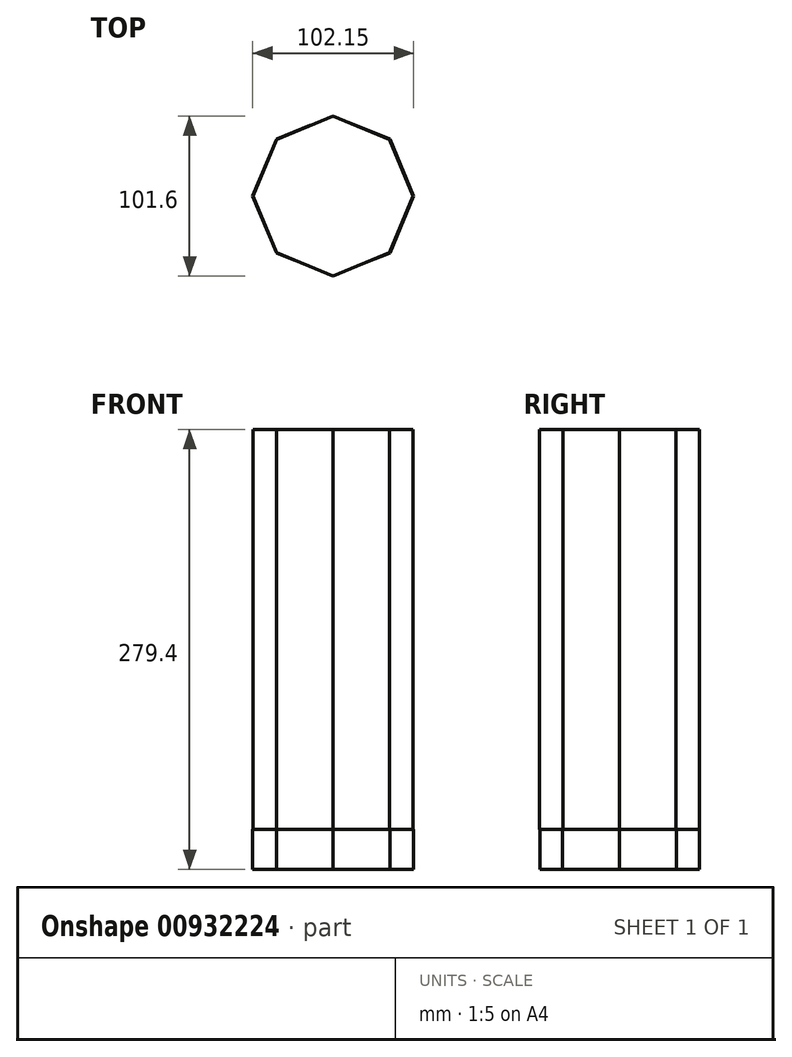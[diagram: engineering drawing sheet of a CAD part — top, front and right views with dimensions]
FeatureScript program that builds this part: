
annotation { "Feature Type Name" : "Feature", "Feature Type Description" : "" }
export const myFeature = defineFeature(function(context is Context, id is Id, definition is map)
    precondition{}
    {
        {
            var Q0;
            Q0=qCreatedBy(makeId("Top.planeOp"),FACE);
            var sketch = newSketch(context, id + "F0", { "sketchPlane" : qUnion([Q0])});
            skCircle(sketch, "E0.cCircle", {"center": v(0, 0) * mm, "radius": 50.8 * mm, "construction": true});
            skLineSegment(sketch, "E0.0", {"start": v(50.8, 0) * mm, "end": v(35.92, -35.92) * mm});
            skLineSegment(sketch, "E0.1", {"start": v(35.92, -35.92) * mm, "end": v(0, -50.8) * mm});
            skLineSegment(sketch, "E0.2", {"start": v(0, -50.8) * mm, "end": v(-35.92, -35.92) * mm});
            skLineSegment(sketch, "E0.3", {"start": v(-35.92, -35.92) * mm, "end": v(-50.8, 0) * mm});
            skLineSegment(sketch, "E0.4", {"start": v(-50.8, 0) * mm, "end": v(-35.92, 35.92) * mm});
            skLineSegment(sketch, "E0.5", {"start": v(-35.92, 35.92) * mm, "end": v(0, 50.8) * mm});
            skLineSegment(sketch, "E0.6", {"start": v(0, 50.8) * mm, "end": v(35.92, 35.92) * mm});
            skLineSegment(sketch, "E0.7", {"start": v(35.92, 35.92) * mm, "end": v(50.8, 0) * mm});
            skSolve(sketch);
        }
        {
            var Q0;
            Q0=makeQuery(id+"F0.imprint","IMPRINT",FACE,{"disambiguationData":[TD([[makeQuery(id+"F0.imprint","IMPRINT",EDGE,{"derivedFrom":sQuery(id+"F0.wireOp",EDGE,"E0.0")}),-1.0]])]});
            extrude(context, id + "F1", {"entities" : qUnion([Q0]), "depth" : 254 * mm, "offsetDistance" : 25.4 * mm});
        }
        {
            var Q0;
            Q0=qCreatedBy(makeId("Top.planeOp"),FACE);
            var sketch = newSketch(context, id + "F2", { "sketchPlane" : qUnion([Q0])});
            skLineSegment(sketch, "E1", {"start": v(-35.85, -36.1) * mm, "end": v(0, 0) * mm});
            skLineSegment(sketch, "E2", {"start": v(0, 0) * mm, "end": v(0, -50.45) * mm});
            skLineSegment(sketch, "E3", {"start": v(0, -50.45) * mm, "end": v(-35.85, -36.1) * mm});
            skLineSegment(sketch, "E4", {"start": v(-50.95, 0) * mm, "end": v(-35.85, -36.1) * mm});
            skLineSegment(sketch, "E5", {"start": v(-50.95, 0) * mm, "end": v(0, 0) * mm});
            skLineSegment(sketch, "E6", {"start": v(-50.95, 0) * mm, "end": v(-35.85, 36.1) * mm});
            skLineSegment(sketch, "E7", {"start": v(-35.85, 36.1) * mm, "end": v(0, 0) * mm});
            skLineSegment(sketch, "E8", {"start": v(0, 50.7) * mm, "end": v(-35.85, 36.1) * mm});
            skLineSegment(sketch, "E9", {"start": v(0, 0) * mm, "end": v(0, 50.7) * mm});
            skLineSegment(sketch, "E10", {"start": v(0, 50.7) * mm, "end": v(36.1, 36.1) * mm});
            skLineSegment(sketch, "E11", {"start": v(36.1, 36.1) * mm, "end": v(0, 0) * mm});
            skLineSegment(sketch, "E12", {"start": v(51.2, 0) * mm, "end": v(36.1, 36.1) * mm});
            skLineSegment(sketch, "E13", {"start": v(51.2, 0) * mm, "end": v(36.1, -36.1) * mm});
            skLineSegment(sketch, "E14", {"start": v(36.1, -36.1) * mm, "end": v(0, 0) * mm});
            skLineSegment(sketch, "E15", {"start": v(0, 0) * mm, "end": v(51.2, 0) * mm});
            skLineSegment(sketch, "E16", {"start": v(36.1, -36.1) * mm, "end": v(0, -50.45) * mm});
            skSolve(sketch);
        }
        {
            var Q0;
            Q0 = qSketchRegion(id + "F2", true);
            extrude(context, id + "F3", {"entities" : qUnion([Q0]), "operationType" : NewBodyOperationType.ADD, "oppositeDirection" : true, "depth" : 25.4 * mm, "offsetDistance" : 25.4 * mm});
        }
    });
